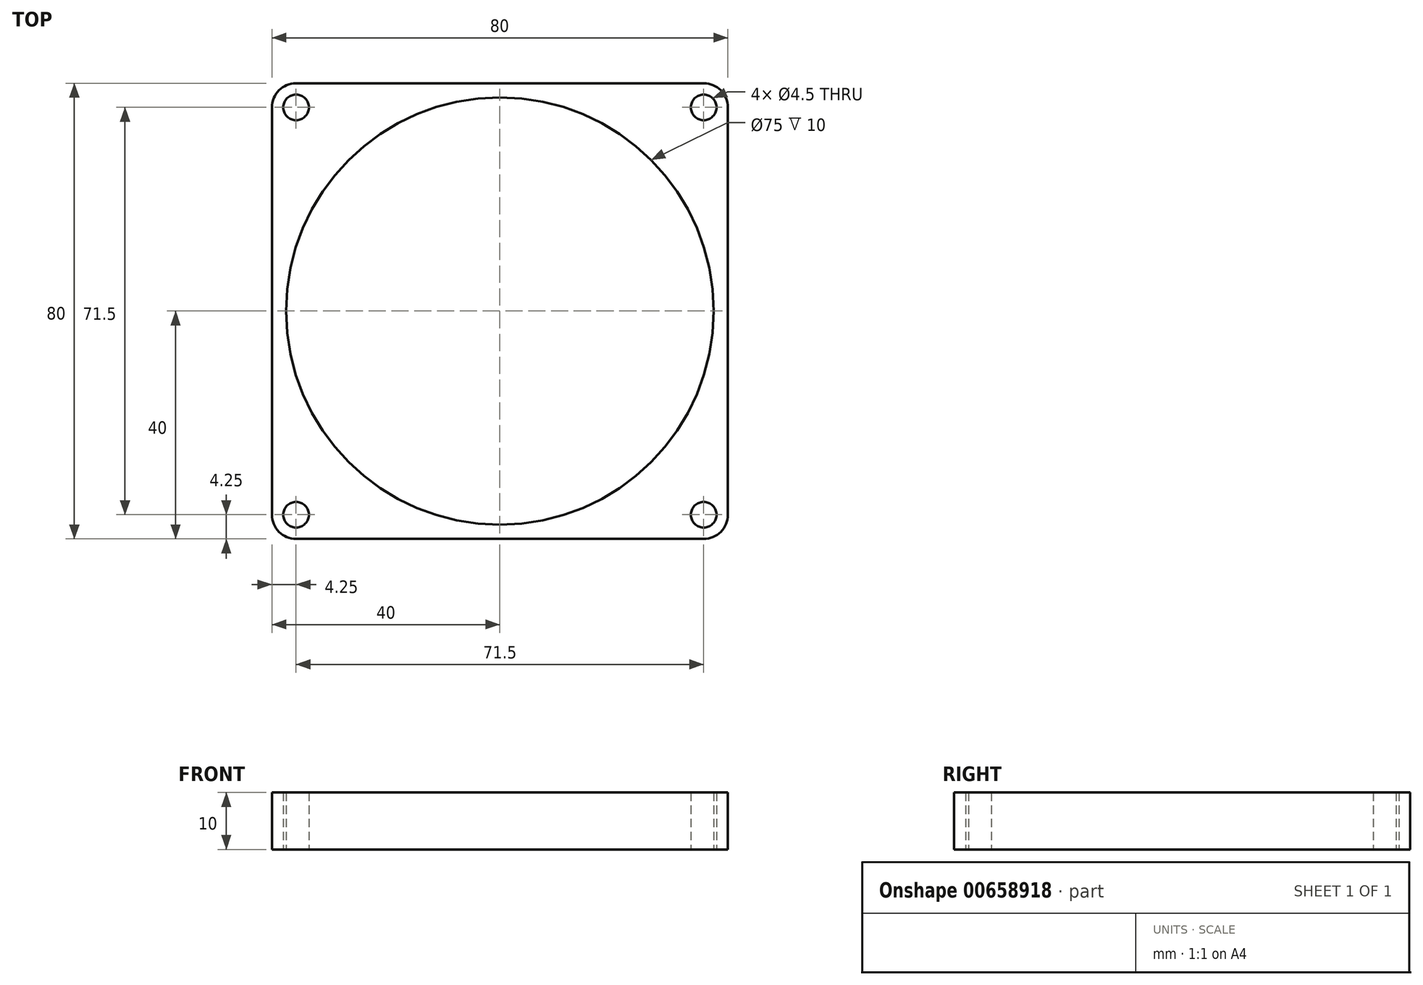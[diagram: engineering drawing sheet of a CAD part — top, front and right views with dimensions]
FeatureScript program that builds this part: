
annotation { "Feature Type Name" : "Feature", "Feature Type Description" : "" }
export const myFeature = defineFeature(function(context is Context, id is Id, definition is map)
    precondition{}
    {
        {
            var Q0;
            Q0=qCreatedBy(makeId("Top.planeOp"),FACE);
            var sketch = newSketch(context, id + "F0", { "sketchPlane" : qUnion([Q0])});
            skLineSegment(sketch, "E0.bottom", {"start": v(0, 0) * mm, "end": v(40, 0) * mm});
            skLineSegment(sketch, "E0.top", {"start": v(0, 40) * mm, "end": v(35.75, 40) * mm});
            skLineSegment(sketch, "E0.left", {"start": v(0, 0) * mm, "end": v(0, 40) * mm});
            skLineSegment(sketch, "E0.right", {"start": v(40, 0) * mm, "end": v(40, 35.75) * mm});
            skLineSegment(sketch, "E1.0", {"start": v(35.75, 0) * mm, "end": v(35.75, 35.75) * mm, "construction": true});
            skLineSegment(sketch, "E1.1", {"start": v(0, 35.75) * mm, "end": v(35.75, 35.75) * mm, "construction": true});
            skCircle(sketch, "E2", {"center": v(35.75, 35.75) * mm, "radius": 2.25 * mm});
            skPoint(sketch, "E3.visualSharp", {"position": v(40, 40) * mm});
            skArc(sketch, "E3.filletArc", {"start": v(40, 35.75) * mm, "mid": v(38.76, 38.76) * mm, "end": v(35.75, 40) * mm});
            skArc(sketch, "E4", {"start": v(37.5, 0) * mm, "mid": v(26.52, 26.52) * mm, "end": v(0, 37.5) * mm});
            skSolve(sketch);
        }
        {
            var Q0;
            {var subQ2=sQuery(id+"F0.wireOp",EDGE,"E0.top");Q0=makeQuery(id+"F0.imprint","IMPRINT",FACE,{"disambiguationData":[TD([[makeQuery(id+"F0.imprint","IMPRINT",EDGE,{"derivedFrom":subQ2}),-1.0]])]});}
            extrude(context, id + "F1", {"entities" : qUnion([Q0]), "depth" : 10 * mm, "offsetDistance" : 25 * mm});
        }
        {
            var Q0;
            Q0=makeQuery(id+"F1.opExtrude","SWEPT_BODY",BODY,{"disambiguationData":[OSD([sQuery(id+"F0.wireOp",EDGE,"E0.bottom"),sQuery(id+"F0.wireOp",EDGE,"E0.top"),sQuery(id+"F0.wireOp",EDGE,"E0.left"),sQuery(id+"F0.wireOp",EDGE,"E0.right"),sQuery(id+"F0.wireOp",EDGE,"E2"),sQuery(id+"F0.wireOp",EDGE,"E3.filletArc"),sQuery(id+"F0.wireOp",EDGE,"E4")])]});
            var Q1;
            Q1=makeQuery(id+"F1.opExtrude","SWEPT_FACE",FACE,{"disambiguationData":[OSD([sQuery(id+"F0.wireOp",EDGE,"E0.bottom")])]});
            mirror(context, id + "F2", {"operationType" : NewBodyOperationType.ADD, "entities" : qUnion([Q0]), "mirrorPlane" : qUnion([Q1])});
        }
        {
            var Q0;
            Q0=makeQuery(id+"F1.opExtrude","SWEPT_BODY",BODY,{"disambiguationData":[OSD([sQuery(id+"F0.wireOp",EDGE,"E0.bottom"),sQuery(id+"F0.wireOp",EDGE,"E0.top"),sQuery(id+"F0.wireOp",EDGE,"E0.left"),sQuery(id+"F0.wireOp",EDGE,"E0.right"),sQuery(id+"F0.wireOp",EDGE,"E2"),sQuery(id+"F0.wireOp",EDGE,"E3.filletArc"),sQuery(id+"F0.wireOp",EDGE,"E4")])]});
            var Q1;
            Q1=makeQuery(id+"F1.opExtrude","SWEPT_FACE",FACE,{"disambiguationData":[OSD([sQuery(id+"F0.wireOp",EDGE,"E0.left")])]});
            mirror(context, id + "F3", {"operationType" : NewBodyOperationType.ADD, "entities" : qUnion([Q0]), "mirrorPlane" : qUnion([Q1])});
        }
    });
